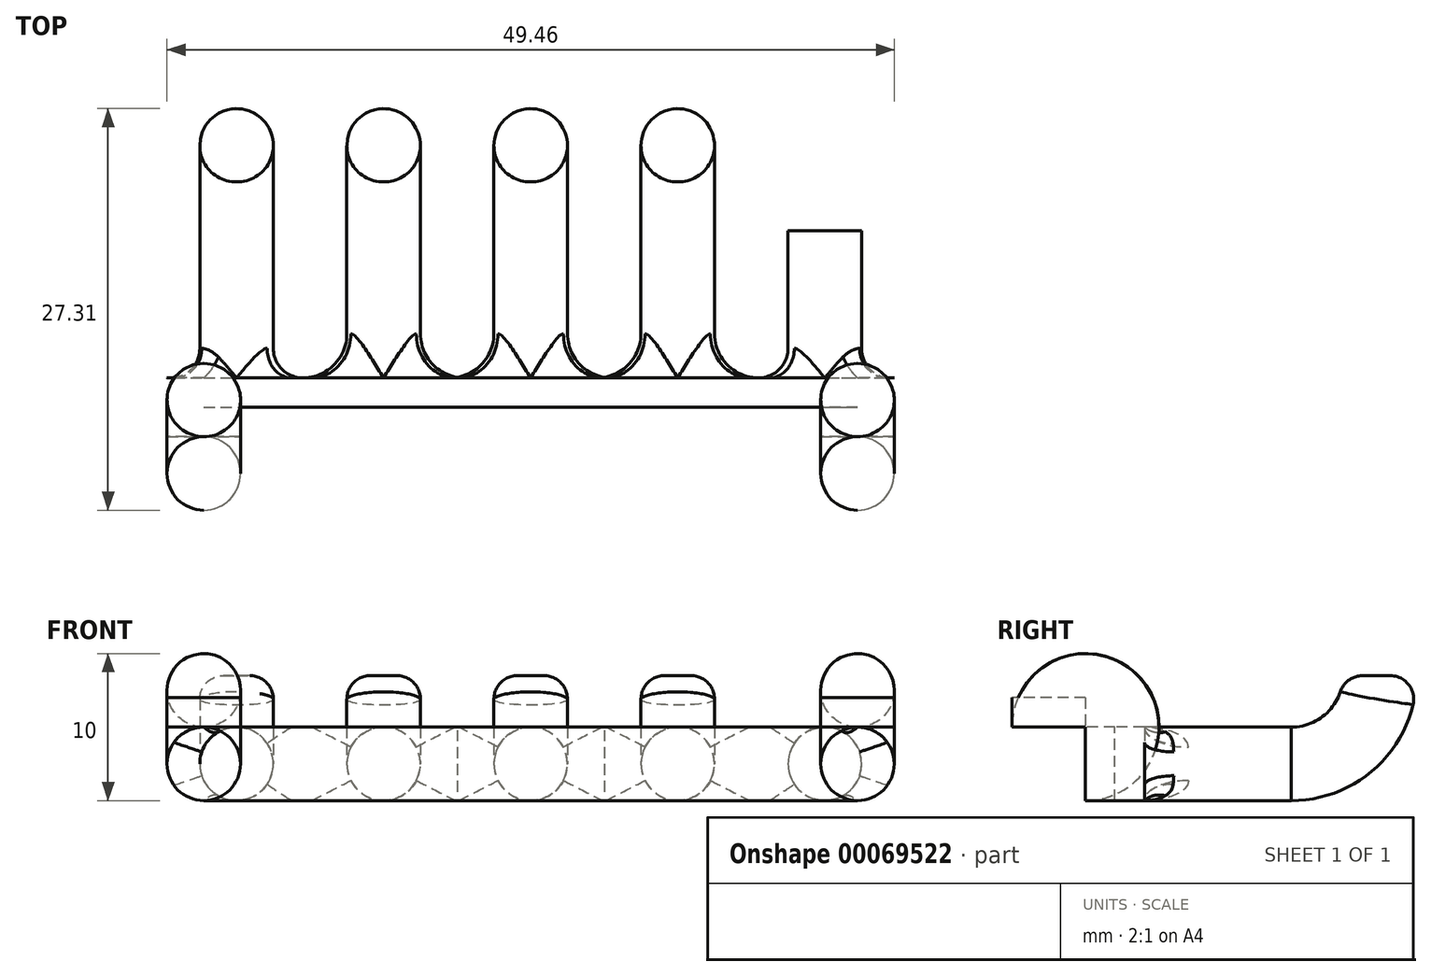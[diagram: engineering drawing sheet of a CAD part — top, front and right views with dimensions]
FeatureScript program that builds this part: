
annotation { "Feature Type Name" : "Feature", "Feature Type Description" : "" }
export const myFeature = defineFeature(function(context is Context, id is Id, definition is map)
    precondition{}
    {
        {
            var Q0;
            Q0=qCreatedBy(makeId("Front.planeOp"),FACE);
            var sketch = newSketch(context, id + "F0", { "sketchPlane" : qUnion([Q0])});
            skLineSegment(sketch, "E0", {"start": v(0, 0) * mm, "end": v(0, 50) * mm, "construction": true});
            skLineSegment(sketch, "E1", {"start": v(0, 0) * mm, "end": v(-22.23, 0) * mm, "construction": true});
            skLineSegment(sketch, "E2.MirrorCS", {"start": v(0, 0) * mm, "end": v(22.23, 0) * mm, "construction": true});
            skCircle(sketch, "E3", {"center": v(-22.23, 0) * mm, "radius": 2.5 * mm});
            skLineSegment(sketch, "E4.bottom", {"start": v(-22.23, -2.5) * mm, "end": v(22.23, -2.5) * mm});
            skLineSegment(sketch, "E4.top", {"start": v(-22.23, 2.5) * mm, "end": v(22.23, 2.5) * mm});
            skLineSegment(sketch, "E4.left", {"start": v(-22.23, -2.5) * mm, "end": v(-22.23, 2.5) * mm});
            skLineSegment(sketch, "E4.right", {"start": v(22.23, -2.5) * mm, "end": v(22.23, 2.5) * mm});
            skPoint(sketch, "E4.middle", {"position": v(0, 0) * mm});
            skCircle(sketch, "E5.MirrorC", {"center": v(22.23, 0) * mm, "radius": 2.5 * mm});
            skSolve(sketch);
        }
        {
            var Q0;
            Q0=qSketchRegion(id+"F0",true);
            var Q1;
            Q1=makeQuery(id+"F0.imprint","IMPRINT",FACE,{"disambiguationData":[TD([[makeQuery(id+"F0.imprint","IMPRINT",EDGE,{"derivedFrom":sQuery(id+"F0.wireOp",EDGE,"E3")}),1.0]])]});
            var Q2;
            Q2=makeQuery(id+"F0.imprint","IMPRINT",FACE,{"disambiguationData":[TD([[makeQuery(id+"F0.imprint","IMPRINT",EDGE,{"derivedFrom":sQuery(id+"F0.wireOp",EDGE,"E5.MirrorC")}),-1.0]])]});
            extrude(context, id + "F1", {"entities" : qUnion([Q0, Q1, Q2]), "oppositeDirection" : true, "depth" : 2 * mm});
        }
        {
            var Q0;
            {var subQ0=sQuery(id+"F0.wireOp",EDGE,"E4.left");Q0=makeQuery(id+"F0.imprint","IMPRINT",FACE,{"disambiguationData":[TD([[makeQuery(id+"F0.imprint","IMPRINT",EDGE,{"derivedFrom":subQ0}),1.0]])]});}
            var Q1;
            {var subQ0=sQuery(id+"F0.wireOp",EDGE,"E4.left");Q1=makeQuery(id+"F0.imprint","IMPRINT",FACE,{"disambiguationData":[TD([[makeQuery(id+"F0.imprint","IMPRINT",EDGE,{"derivedFrom":subQ0}),-1.0]])]});}
            var Q2;
            {var subQ0=sQuery(id+"F0.wireOp",EDGE,"E4.right");Q2=makeQuery(id+"F0.imprint","IMPRINT",FACE,{"disambiguationData":[TD([[makeQuery(id+"F0.imprint","IMPRINT",EDGE,{"derivedFrom":subQ0}),-1.0]])]});}
            var Q3;
            {var subQ0=sQuery(id+"F0.wireOp",EDGE,"E4.right");Q3=makeQuery(id+"F0.imprint","IMPRINT",FACE,{"disambiguationData":[TD([[makeQuery(id+"F0.imprint","IMPRINT",EDGE,{"derivedFrom":subQ0}),1.0]])]});}
            var Q4;
            Q4=sQuery(id+"F0.wireOp",EDGE,"E5.MirrorC");
            var Q5;
            Q5=sQuery(id+"F0.wireOp",EDGE,"E4.left");
            var Q6;
            Q6=sQuery(id+"F0.wireOp",EDGE,"E3");
            extrude(context, id + "F2", {"entities" : qUnion([Q0, Q1, Q2, Q3]), "operationType" : NewBodyOperationType.ADD, "surfaceEntities" : qUnion([Q4, Q5, Q6]), "depth" : 2 * mm});
        }
        {
            var Q0;
            Q0=makeQuery(id+"F2.opExtrude","CAP_FACE",FACE,{"disambiguationData":[OSD([sQuery(id+"F0.wireOp",EDGE,"E3")])],"isStart":false});
            var sketch = newSketch(context, id + "F3", { "sketchPlane" : qUnion([Q0])});
            skLineSegment(sketch, "E6", {"start": v(-22.23, 2.5) * mm, "end": v(22.66, 2.5) * mm, "construction": true});
            skSolve(sketch);
        }
        {
            var Q0;
            Q0=makeQuery(id+"F3.imprint","IMPRINT",FACE,{"disambiguationData":[TD([[makeQuery(id+"F3.imprint","IMPRINT",EDGE,{"derivedFrom":makeQuery(id+"F2.opExtrude","CAP_EDGE",EDGE,{"disambiguationData":[OSD([sQuery(id+"F0.wireOp",EDGE,"E3")])],"isStart":false})}),1.0]])]});
            var Q1;
            Q1=makeQuery(id+"F2.opExtrude","CAP_FACE",FACE,{"disambiguationData":[OSD([sQuery(id+"F0.wireOp",EDGE,"E5.MirrorC")])],"isStart":false});
            var Q2;
            Q2=sQuery(id+"F3.wireOp",EDGE,"E6");
            revolve(context, id + "F4", {"operationType" : NewBodyOperationType.ADD, "entities" : qUnion([Q0, Q1]), "axis" : qUnion([Q2]), "revolveType" : RevolveType.ONE_DIRECTION, "oppositeDirection" : true, "angle" : 90 * degree});
        }
        {
            var Q0;
            Q0=makeQuery(id+"F4.opRevolve","CAP_FACE",FACE,{"disambiguationData":[OSD([sQuery(id+"F0.wireOp",EDGE,"E3")])],"isStart":false});
            var Q1;
            Q1=makeQuery(id+"F4.opRevolve","CAP_FACE",FACE,{"disambiguationData":[OSD([sQuery(id+"F0.wireOp",EDGE,"E5.MirrorC")])],"isStart":false});
            extrude(context, id + "F5", {"entities" : qUnion([Q0, Q1]), "operationType" : NewBodyOperationType.ADD, "depth" : 2 * mm});
        }
        {
            var Q0;
            Q0=makeQuery(id+"F1.opExtrude","CAP_FACE",FACE,{"disambiguationData":[OSD([sQuery(id+"F0.wireOp",EDGE,"E3"),sQuery(id+"F0.wireOp",EDGE,"E4.bottom"),sQuery(id+"F0.wireOp",EDGE,"E4.top"),sQuery(id+"F0.wireOp",EDGE,"E5.MirrorC")])],"isStart":false});
            var sketch = newSketch(context, id + "F6", { "sketchPlane" : qUnion([Q0])});
            skCircle(sketch, "E7", {"center": v(0, 0) * mm, "radius": 2.5 * mm});
            skCircle(sketch, "E8.1.0.0", {"center": v(10, 0) * mm, "radius": 2.5 * mm});
            skCircle(sketch, "E8.2.0.0", {"center": v(20, 0) * mm, "radius": 2.5 * mm});
            skLineSegment(sketch, "E8.direction1", {"start": v(0, 0) * mm, "end": v(10, 0) * mm, "construction": true});
            skCircle(sketch, "E9.MirrorC", {"center": v(-10, 0) * mm, "radius": 2.5 * mm});
            skCircle(sketch, "E10.MirrorC", {"center": v(-20, 0) * mm, "radius": 2.5 * mm});
            skSolve(sketch);
        }
        {
            var Q0;
            Q0 = qSketchRegion(id + "F6", true);
            extrude(context, id + "F7", {"entities" : qUnion([Q0]), "operationType" : NewBodyOperationType.ADD, "depth" : 10 * mm});
        }
        {
            var Q0;
            Q0=makeQuery(id+"F7.opExtrude","CAP_FACE",FACE,{"disambiguationData":[OSD([sQuery(id+"F6.wireOp",EDGE,"E10.MirrorC")])],"isStart":false});
            var sketch = newSketch(context, id + "F8", { "sketchPlane" : qUnion([Q0])});
            skLineSegment(sketch, "E11", {"start": v(0, 0) * mm, "end": v(0, 6) * mm, "construction": true});
            skLineSegment(sketch, "E12", {"start": v(0, 6) * mm, "end": v(-20, 6) * mm, "construction": true});
            skSolve(sketch);
        }
        {
            var Q0;
            Q0=makeQuery(id+"F7.opExtrude","CAP_FACE",FACE,{"disambiguationData":[OSD([sQuery(id+"F6.wireOp",EDGE,"E8.2.0.0")])],"isStart":false});
            var Q1;
            Q1=makeQuery(id+"F7.opExtrude","CAP_FACE",FACE,{"disambiguationData":[OSD([sQuery(id+"F6.wireOp",EDGE,"E9.MirrorC")])],"isStart":false});
            var Q2;
            Q2=makeQuery(id+"F7.opExtrude","CAP_FACE",FACE,{"disambiguationData":[OSD([sQuery(id+"F6.wireOp",EDGE,"E8.1.0.0")])],"isStart":false});
            var Q3;
            Q3=makeQuery(id+"F7.opExtrude","CAP_FACE",FACE,{"disambiguationData":[OSD([sQuery(id+"F6.wireOp",EDGE,"E7")])],"isStart":false});
            var Q4;
            Q4=makeQuery(id+"F8.imprint","IMPRINT",FACE,{"disambiguationData":[TD([[makeQuery(id+"F8.imprint","IMPRINT",EDGE,{"derivedFrom":makeQuery(id+"F7.opExtrude","CAP_EDGE",EDGE,{"disambiguationData":[OSD([sQuery(id+"F6.wireOp",EDGE,"E10.MirrorC")])],"isStart":false})}),-1.0]])]});
            var Q5;
            Q5=sQuery(id+"F8.wireOp",EDGE,"E12");
            revolve(context, id + "F9", {"operationType" : NewBodyOperationType.ADD, "entities" : qUnion([Q0, Q1, Q2, Q3, Q4]), "axis" : qUnion([Q5]), "revolveType" : RevolveType.ONE_DIRECTION, "angle" : 90 * degree});
        }
        {
            var Q0;
            Q0=makeQuery(id+"F7.boolean.opBoolean","SPLIT",EDGE,{"disambiguationData":[OD(0.0)],"derivedFrom":makeQuery(id+"F7.opExtrude","CAP_EDGE",EDGE,{"disambiguationData":[OSD([sQuery(id+"F6.wireOp",EDGE,"E10.MirrorC")])],"isStart":true})});
            var Q1;
            Q1=makeQuery(id+"F7.boolean.opBoolean","SPLIT",EDGE,{"disambiguationData":[OD(1.0)],"derivedFrom":makeQuery(id+"F7.opExtrude","CAP_EDGE",EDGE,{"disambiguationData":[OSD([sQuery(id+"F6.wireOp",EDGE,"E8.2.0.0")])],"isStart":true})});
            fillet(context, id + "F10", {"entities" : qUnion([Q0, Q1]), "radius" : 2 * mm, "tangentPropagation" : true, "allowEdgeOverflow" : false});
        }
        {
            var Q0;
            Q0=makeQuery(id+"F7.boolean.opBoolean","SPLIT",EDGE,{"disambiguationData":[OD(0.0)],"derivedFrom":makeQuery(id+"F7.opExtrude","CAP_EDGE",EDGE,{"disambiguationData":[OSD([sQuery(id+"F6.wireOp",EDGE,"E8.1.0.0")])],"isStart":true})});
            var Q1;
            Q1=makeQuery(id+"F7.boolean.opBoolean","SPLIT",EDGE,{"disambiguationData":[OD(1.0)],"derivedFrom":makeQuery(id+"F7.opExtrude","CAP_EDGE",EDGE,{"disambiguationData":[OSD([sQuery(id+"F6.wireOp",EDGE,"E7")])],"isStart":true})});
            var Q2;
            Q2=makeQuery(id+"F7.boolean.opBoolean","SPLIT",EDGE,{"disambiguationData":[OD(1.0)],"derivedFrom":makeQuery(id+"F7.opExtrude","CAP_EDGE",EDGE,{"disambiguationData":[OSD([sQuery(id+"F6.wireOp",EDGE,"E9.MirrorC")])],"isStart":true})});
            fillet(context, id + "F11", {"entities" : qUnion([Q0, Q1, Q2]), "radius" : 3 * mm, "tangentPropagation" : true, "allowEdgeOverflow" : false});
        }
        {
            var Q0;
            Q0=makeQuery(id+"F9.opRevolve","CAP_EDGE",EDGE,{"disambiguationData":[OSD([sQuery(id+"F6.wireOp",EDGE,"E8.1.0.0")])],"isStart":false});
            var Q1;
            Q1=makeQuery(id+"F9.opRevolve","CAP_EDGE",EDGE,{"disambiguationData":[OSD([sQuery(id+"F6.wireOp",EDGE,"E8.2.0.0")])],"isStart":false});
            var Q2;
            Q2=makeQuery(id+"F9.opRevolve","CAP_EDGE",EDGE,{"disambiguationData":[OSD([sQuery(id+"F6.wireOp",EDGE,"E7")])],"isStart":false});
            var Q3;
            Q3=makeQuery(id+"F9.opRevolve","CAP_EDGE",EDGE,{"disambiguationData":[OSD([sQuery(id+"F6.wireOp",EDGE,"E9.MirrorC")])],"isStart":false});
            var Q4;
            Q4=makeQuery(id+"F9.opRevolve","CAP_EDGE",EDGE,{"disambiguationData":[OSD([sQuery(id+"F6.wireOp",EDGE,"E10.MirrorC")])],"isStart":false});
            fillet(context, id + "F12", {"entities" : qUnion([Q0, Q1, Q2, Q3, Q4]), "radius" : 1.6 * mm, "tangentPropagation" : true, "allowEdgeOverflow" : false});
        }
    });
